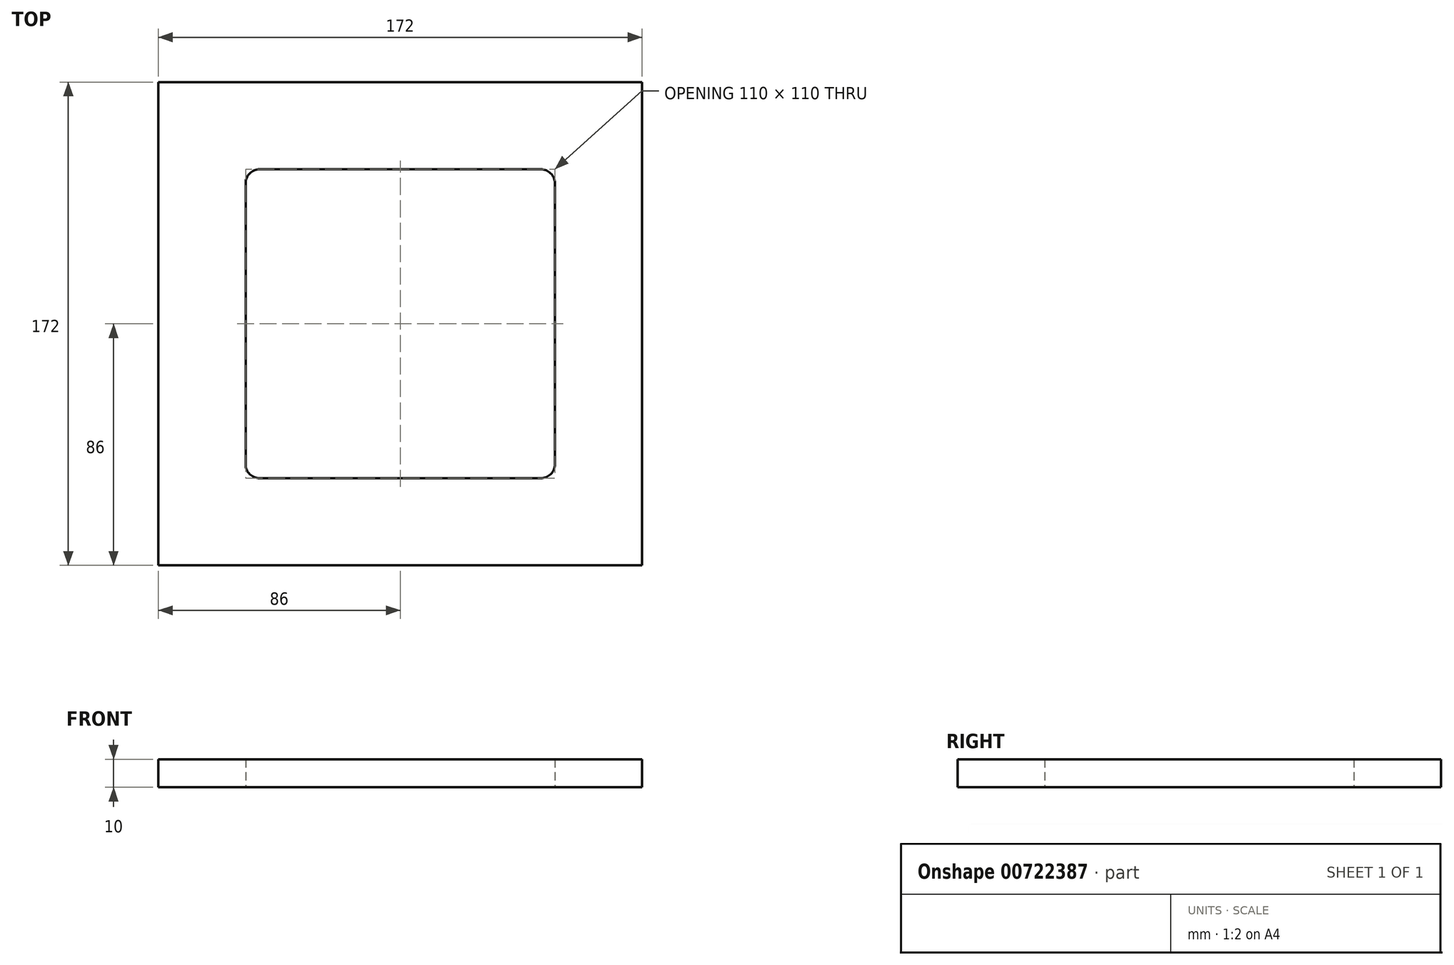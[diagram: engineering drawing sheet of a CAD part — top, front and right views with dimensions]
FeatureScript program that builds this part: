
annotation { "Feature Type Name" : "Feature", "Feature Type Description" : "" }
export const myFeature = defineFeature(function(context is Context, id is Id, definition is map)
    precondition{}
    {
        {
            var Q0;
            Q0=qCreatedBy(makeId("Top.planeOp"),FACE);
            var sketch = newSketch(context, id + "F0", { "sketchPlane" : qUnion([Q0])});
            skLineSegment(sketch, "E0.bottom", {"start": v(-86, 86) * mm, "end": v(86, 86) * mm});
            skLineSegment(sketch, "E0.top", {"start": v(-86, -86) * mm, "end": v(86, -86) * mm});
            skLineSegment(sketch, "E0.left", {"start": v(-86, 86) * mm, "end": v(-86, -86) * mm});
            skLineSegment(sketch, "E0.right", {"start": v(86, 86) * mm, "end": v(86, -86) * mm});
            skPoint(sketch, "E0.middle", {"position": v(0, 0) * mm});
            skSolve(sketch);
        }
        {
            var Q0;
            Q0 = qSketchRegion(id + "F0", true);
            extrude(context, id + "F1", {"entities" : qUnion([Q0]), "depth" : 10 * mm, "offsetDistance" : 25 * mm});
        }
        {
            var Q0;
            Q0=qCreatedBy(makeId("Top.planeOp"),FACE);
            var sketch = newSketch(context, id + "F2", { "sketchPlane" : qUnion([Q0])});
            skLineSegment(sketch, "E1.bottom", {"start": v(-55, 55) * mm, "end": v(55, 55) * mm});
            skLineSegment(sketch, "E1.top", {"start": v(-55, -55) * mm, "end": v(55, -55) * mm});
            skLineSegment(sketch, "E1.left", {"start": v(-55, 55) * mm, "end": v(-55, -55) * mm});
            skLineSegment(sketch, "E1.right", {"start": v(55, 55) * mm, "end": v(55, -55) * mm});
            skPoint(sketch, "E1.middle", {"position": v(0, 0) * mm});
            skSolve(sketch);
        }
        {
            var Q0;
            Q0 = qSketchRegion(id + "F2", true);
            extrude(context, id + "F3", {"entities" : qUnion([Q0]), "operationType" : NewBodyOperationType.REMOVE, "depth" : 45 * mm, "offsetDistance" : 25 * mm});
        }
        {
            var Q0;
            Q0=makeQuery(id+"F3.boolean.opBoolean","COPY",EDGE,{"derivedFrom":makeQuery(id+"F3.opExtrude","SWEPT_EDGE",EDGE,{"disambiguationData":[OSD([sQuery(id+"F2.wireOp",EDGE,"E1.bottom"),sQuery(id+"F2.wireOp",EDGE,"E1.right")])]})});
            var Q1;
            Q1=makeQuery(id+"F3.boolean.opBoolean","COPY",EDGE,{"derivedFrom":makeQuery(id+"F3.opExtrude","SWEPT_EDGE",EDGE,{"disambiguationData":[OSD([sQuery(id+"F2.wireOp",EDGE,"E1.top"),sQuery(id+"F2.wireOp",EDGE,"E1.right")])]})});
            var Q2;
            Q2=makeQuery(id+"F3.boolean.opBoolean","COPY",EDGE,{"derivedFrom":makeQuery(id+"F3.opExtrude","SWEPT_EDGE",EDGE,{"disambiguationData":[OSD([sQuery(id+"F2.wireOp",EDGE,"E1.top"),sQuery(id+"F2.wireOp",EDGE,"E1.left")])]})});
            var Q3;
            Q3=makeQuery(id+"F3.boolean.opBoolean","COPY",EDGE,{"derivedFrom":makeQuery(id+"F3.opExtrude","SWEPT_EDGE",EDGE,{"disambiguationData":[OSD([sQuery(id+"F2.wireOp",EDGE,"E1.bottom"),sQuery(id+"F2.wireOp",EDGE,"E1.left")])]})});
            fillet(context, id + "F4", {"entities" : qUnion([Q0, Q1, Q2, Q3]), "radius" : 5 * mm, "tangentPropagation" : true, "allowEdgeOverflow" : false});
        }
    });
